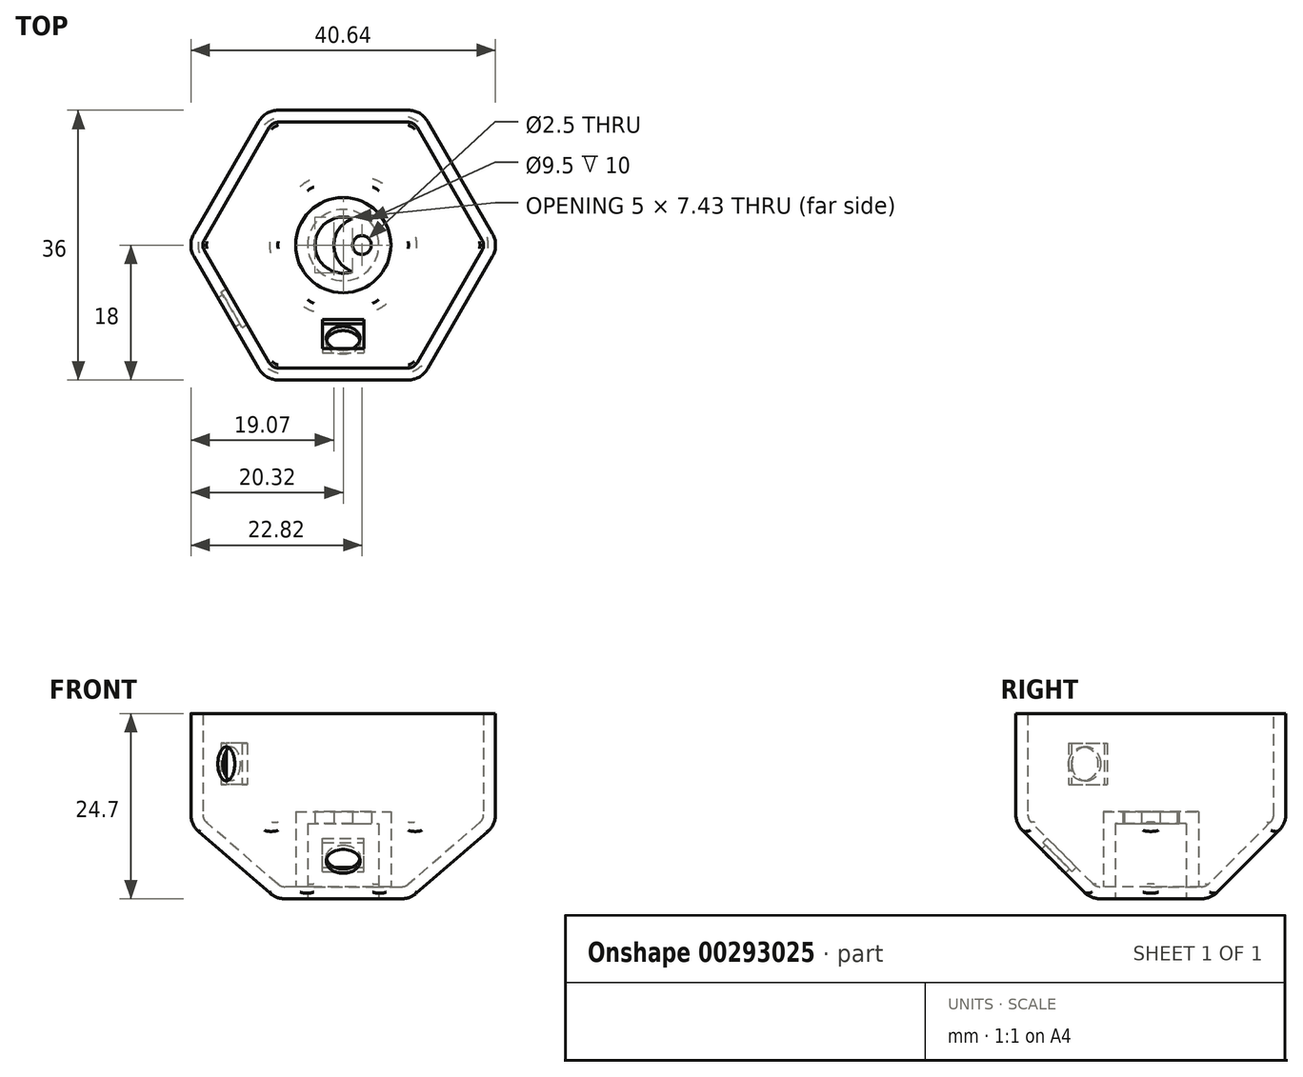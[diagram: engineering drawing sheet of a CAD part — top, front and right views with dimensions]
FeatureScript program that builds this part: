
annotation { "Feature Type Name" : "Feature", "Feature Type Description" : "" }
export const myFeature = defineFeature(function(context is Context, id is Id, definition is map)
    precondition{}
    {
        {
            var Q0;
            Q0=qCreatedBy(makeId("Top.planeOp"),FACE);
            var sketch = newSketch(context, id + "F0", { "sketchPlane" : qUnion([Q0])});
            skCircle(sketch, "E0.cCircle", {"center": v(0, 0) * mm, "radius": 18 * mm, "construction": true});
            skLineSegment(sketch, "E0.0", {"start": v(-10.4, 18) * mm, "end": v(10.4, 18) * mm});
            skLineSegment(sketch, "E0.1", {"start": v(10.4, 18) * mm, "end": v(20.78, 0) * mm});
            skLineSegment(sketch, "E0.2", {"start": v(20.78, 0) * mm, "end": v(10.4, -18) * mm});
            skLineSegment(sketch, "E0.3", {"start": v(10.4, -18) * mm, "end": v(-10.4, -18) * mm});
            skLineSegment(sketch, "E0.4", {"start": v(-10.4, -18) * mm, "end": v(-20.78, 0) * mm});
            skLineSegment(sketch, "E0.5", {"start": v(-20.78, 0) * mm, "end": v(-10.4, 18) * mm});
            skPoint(sketch, "E0.0.midPoint", {"position": v(0, 18) * mm});
            skSolve(sketch);
        }
        {
            var Q0;
            Q0 = qSketchRegion(id + "F0", true);
            extrude(context, id + "F1", {"entities" : qUnion([Q0]), "endBound" : BoundingType.SYMMETRIC, "depth" : 36 * mm});
        }
        {
            var Q0;
            Q0=makeQuery(id+"F1.opExtrude","CAP_FACE",FACE,{"disambiguationData":[OSD([sQuery(id+"F0.wireOp",EDGE,"E0.0"),sQuery(id+"F0.wireOp",EDGE,"E0.1"),sQuery(id+"F0.wireOp",EDGE,"E0.2"),sQuery(id+"F0.wireOp",EDGE,"E0.3"),sQuery(id+"F0.wireOp",EDGE,"E0.4"),sQuery(id+"F0.wireOp",EDGE,"E0.5")])],"isStart":false});
            var Q1;
            Q1=makeQuery(id+"F1.opExtrude","CAP_FACE",FACE,{"disambiguationData":[OSD([sQuery(id+"F0.wireOp",EDGE,"E0.0"),sQuery(id+"F0.wireOp",EDGE,"E0.1"),sQuery(id+"F0.wireOp",EDGE,"E0.2"),sQuery(id+"F0.wireOp",EDGE,"E0.3"),sQuery(id+"F0.wireOp",EDGE,"E0.4"),sQuery(id+"F0.wireOp",EDGE,"E0.5")])],"isStart":true});
            chamfer(context, id + "F2", {"entities" : qUnion([Q0, Q1]), "chamferType" : ChamferType.OFFSET_ANGLE, "width" : 10 * mm, "oppositeDirection" : false, "angle" : 45 * degree, "tangentPropagation" : true});
        }
        {
            var Q0;
            Q0=makeQuery(id+"F1.opExtrude","CAP_FACE",FACE,{"disambiguationData":[OSD([sQuery(id+"F0.wireOp",EDGE,"E0.0"),sQuery(id+"F0.wireOp",EDGE,"E0.1"),sQuery(id+"F0.wireOp",EDGE,"E0.2"),sQuery(id+"F0.wireOp",EDGE,"E0.3"),sQuery(id+"F0.wireOp",EDGE,"E0.4"),sQuery(id+"F0.wireOp",EDGE,"E0.5")])],"isStart":true});
            var sketch = newSketch(context, id + "F3", { "sketchPlane" : qUnion([Q0])});
            skCircle(sketch, "E1", {"center": v(0, 0) * mm, "radius": 4.75 * mm});
            skSolve(sketch);
        }
        {
            var Q0;
            Q0 = qSketchRegion(id + "F3", true);
            extrude(context, id + "F4", {"entities" : qUnion([Q0]), "operationType" : NewBodyOperationType.REMOVE, "oppositeDirection" : true, "depth" : 10 * mm});
        }
        {
            var Q0;
            Q0=makeQuery(id+"F4.boolean.opBoolean","COPY",FACE,{"derivedFrom":makeQuery(id+"F4.opExtrude","CAP_FACE",FACE,{"disambiguationData":[OSD([sQuery(id+"F3.wireOp",EDGE,"E1")])],"isStart":false})});
            var sketch = newSketch(context, id + "F5", { "sketchPlane" : qUnion([Q0])});
            skCircle(sketch, "E2", {"center": v(2.5, 0) * mm, "radius": 1.25 * mm});
            skSolve(sketch);
        }
        {
            var Q0;
            Q0 = qSketchRegion(id + "F5", true);
            extrude(context, id + "F6", {"entities" : qUnion([Q0]), "operationType" : NewBodyOperationType.REMOVE, "oppositeDirection" : true, "depth" : 60 * mm});
        }
        {
            var Q0;
            {var subQ0=sQuery(id+"F0.wireOp",EDGE,"E0.3");Q0=makeQuery(id+"F2.opChamfer","BLEND_FACE",FACE,{"disambiguationData":[OSD([subQ0]),TDD([makeQuery(id+"F1.opExtrude","CAP_EDGE",EDGE,{"disambiguationData":[OSD([subQ0])],"isStart":true})])]});}
            var sketch = newSketch(context, id + "F7", { "sketchPlane" : qUnion([Q0])});
            skCircle(sketch, "E3", {"center": v(0, 0) * mm, "radius": 2.25 * mm});
            skSolve(sketch);
        }
        {
            var Q0;
            Q0=makeQuery(id+"F1.opExtrude","SWEPT_FACE",FACE,{"disambiguationData":[OSD([sQuery(id+"F0.wireOp",EDGE,"E0.4")])]});
            var sketch = newSketch(context, id + "F8", { "sketchPlane" : qUnion([Q0])});
            skCircle(sketch, "E4", {"center": v(0, 0) * mm, "radius": 2.25 * mm});
            skSolve(sketch);
        }
        {
            var Q0;
            {var subQ0=sQuery(id+"F0.wireOp",EDGE,"E0.4");Q0=makeQuery(id+"F2.opChamfer","BLEND_EDGE",EDGE,{"blendedFrom":[makeQuery(id+"F1.opExtrude","CAP_EDGE",EDGE,{"disambiguationData":[OSD([subQ0])],"isStart":false}),makeQuery(id+"F1.opExtrude","SWEPT_FACE",FACE,{"disambiguationData":[OSD([subQ0])]})],"blendedInto":[makeQuery(id+"F1.opExtrude","SWEPT_FACE",FACE,{"disambiguationData":[OSD([subQ0])]})]});}
            var Q1;
            {var subQ0=sQuery(id+"F0.wireOp",EDGE,"E0.3");Q1=makeQuery(id+"F2.opChamfer","BLEND_EDGE",EDGE,{"blendedFrom":[makeQuery(id+"F1.opExtrude","CAP_EDGE",EDGE,{"disambiguationData":[OSD([subQ0])],"isStart":false}),makeQuery(id+"F1.opExtrude","SWEPT_FACE",FACE,{"disambiguationData":[OSD([subQ0])]})],"blendedInto":[makeQuery(id+"F1.opExtrude","SWEPT_FACE",FACE,{"disambiguationData":[OSD([subQ0])]})]});}
            var Q2;
            {var subQ0=sQuery(id+"F0.wireOp",EDGE,"E0.5");Q2=makeQuery(id+"F2.opChamfer","BLEND_EDGE",EDGE,{"blendedFrom":[makeQuery(id+"F1.opExtrude","CAP_EDGE",EDGE,{"disambiguationData":[OSD([subQ0])],"isStart":false}),makeQuery(id+"F1.opExtrude","SWEPT_FACE",FACE,{"disambiguationData":[OSD([subQ0])]})],"blendedInto":[makeQuery(id+"F1.opExtrude","SWEPT_FACE",FACE,{"disambiguationData":[OSD([subQ0])]})]});}
            var Q3;
            {var subQ0=sQuery(id+"F0.wireOp",EDGE,"E0.0");Q3=makeQuery(id+"F2.opChamfer","BLEND_EDGE",EDGE,{"blendedFrom":[makeQuery(id+"F1.opExtrude","CAP_EDGE",EDGE,{"disambiguationData":[OSD([subQ0])],"isStart":false}),makeQuery(id+"F1.opExtrude","SWEPT_FACE",FACE,{"disambiguationData":[OSD([subQ0])]})],"blendedInto":[makeQuery(id+"F1.opExtrude","SWEPT_FACE",FACE,{"disambiguationData":[OSD([subQ0])]})]});}
            var Q4;
            {var subQ0=sQuery(id+"F0.wireOp",EDGE,"E0.1");Q4=makeQuery(id+"F2.opChamfer","BLEND_EDGE",EDGE,{"blendedFrom":[makeQuery(id+"F1.opExtrude","CAP_EDGE",EDGE,{"disambiguationData":[OSD([subQ0])],"isStart":false}),makeQuery(id+"F1.opExtrude","SWEPT_FACE",FACE,{"disambiguationData":[OSD([subQ0])]})],"blendedInto":[makeQuery(id+"F1.opExtrude","SWEPT_FACE",FACE,{"disambiguationData":[OSD([subQ0])]})]});}
            var Q5;
            {var subQ0=sQuery(id+"F0.wireOp",EDGE,"E0.2");Q5=makeQuery(id+"F2.opChamfer","BLEND_EDGE",EDGE,{"blendedFrom":[makeQuery(id+"F1.opExtrude","CAP_EDGE",EDGE,{"disambiguationData":[OSD([subQ0])],"isStart":false}),makeQuery(id+"F1.opExtrude","SWEPT_FACE",FACE,{"disambiguationData":[OSD([subQ0])]})],"blendedInto":[makeQuery(id+"F1.opExtrude","SWEPT_FACE",FACE,{"disambiguationData":[OSD([subQ0])]})]});}
            var Q6;
            {var subQ0=sQuery(id+"F0.wireOp",EDGE,"E0.2");Q6=makeQuery(id+"F2.opChamfer","BLEND_EDGE",EDGE,{"blendedFrom":[makeQuery(id+"F1.opExtrude","CAP_EDGE",EDGE,{"disambiguationData":[OSD([subQ0])],"isStart":true}),makeQuery(id+"F1.opExtrude","SWEPT_FACE",FACE,{"disambiguationData":[OSD([subQ0])]})],"blendedInto":[makeQuery(id+"F1.opExtrude","SWEPT_FACE",FACE,{"disambiguationData":[OSD([subQ0])]})]});}
            var Q7;
            {var subQ0=sQuery(id+"F0.wireOp",EDGE,"E0.3");Q7=makeQuery(id+"F2.opChamfer","BLEND_EDGE",EDGE,{"blendedFrom":[makeQuery(id+"F1.opExtrude","CAP_EDGE",EDGE,{"disambiguationData":[OSD([subQ0])],"isStart":true}),makeQuery(id+"F1.opExtrude","SWEPT_FACE",FACE,{"disambiguationData":[OSD([subQ0])]})],"blendedInto":[makeQuery(id+"F1.opExtrude","SWEPT_FACE",FACE,{"disambiguationData":[OSD([subQ0])]})]});}
            var Q8;
            {var subQ0=sQuery(id+"F0.wireOp",EDGE,"E0.4");Q8=makeQuery(id+"F2.opChamfer","BLEND_EDGE",EDGE,{"blendedFrom":[makeQuery(id+"F1.opExtrude","CAP_EDGE",EDGE,{"disambiguationData":[OSD([subQ0])],"isStart":true}),makeQuery(id+"F1.opExtrude","SWEPT_FACE",FACE,{"disambiguationData":[OSD([subQ0])]})],"blendedInto":[makeQuery(id+"F1.opExtrude","SWEPT_FACE",FACE,{"disambiguationData":[OSD([subQ0])]})]});}
            var Q9;
            {var subQ0=sQuery(id+"F0.wireOp",EDGE,"E0.5");Q9=makeQuery(id+"F2.opChamfer","BLEND_EDGE",EDGE,{"blendedFrom":[makeQuery(id+"F1.opExtrude","CAP_EDGE",EDGE,{"disambiguationData":[OSD([subQ0])],"isStart":true}),makeQuery(id+"F1.opExtrude","SWEPT_FACE",FACE,{"disambiguationData":[OSD([subQ0])]})],"blendedInto":[makeQuery(id+"F1.opExtrude","SWEPT_FACE",FACE,{"disambiguationData":[OSD([subQ0])]})]});}
            var Q10;
            {var subQ0=sQuery(id+"F0.wireOp",EDGE,"E0.0");Q10=makeQuery(id+"F2.opChamfer","BLEND_EDGE",EDGE,{"blendedFrom":[makeQuery(id+"F1.opExtrude","CAP_EDGE",EDGE,{"disambiguationData":[OSD([subQ0])],"isStart":true}),makeQuery(id+"F1.opExtrude","SWEPT_FACE",FACE,{"disambiguationData":[OSD([subQ0])]})],"blendedInto":[makeQuery(id+"F1.opExtrude","SWEPT_FACE",FACE,{"disambiguationData":[OSD([subQ0])]})]});}
            var Q11;
            {var subQ0=sQuery(id+"F0.wireOp",EDGE,"E0.1");Q11=makeQuery(id+"F2.opChamfer","BLEND_EDGE",EDGE,{"blendedFrom":[makeQuery(id+"F1.opExtrude","CAP_EDGE",EDGE,{"disambiguationData":[OSD([subQ0])],"isStart":true}),makeQuery(id+"F1.opExtrude","SWEPT_FACE",FACE,{"disambiguationData":[OSD([subQ0])]})],"blendedInto":[makeQuery(id+"F1.opExtrude","SWEPT_FACE",FACE,{"disambiguationData":[OSD([subQ0])]})]});}
            fillet(context, id + "F9", {"entities" : qUnion([Q0, Q1, Q2, Q3, Q4, Q5, Q6, Q7, Q8, Q9, Q10, Q11]), "radius" : 3 * mm, "tangentPropagation" : true, "allowEdgeOverflow" : false});
        }
        {
            var Q0;
            Q0=makeQuery(id+"F2.opChamfer","BLEND_EDGE",EDGE,{"blendedFrom":[makeQuery(id+"F1.opExtrude","CAP_EDGE",EDGE,{"disambiguationData":[OSD([sQuery(id+"F0.wireOp",EDGE,"E0.4")])],"isStart":true}),makeQuery(id+"F1.opExtrude","CAP_EDGE",EDGE,{"disambiguationData":[OSD([sQuery(id+"F0.wireOp",EDGE,"E0.5")])],"isStart":true})],"blendedInto":[]});
            var Q1;
            Q1=makeQuery(id+"F2.opChamfer","BLEND_EDGE",EDGE,{"blendedFrom":[makeQuery(id+"F1.opExtrude","CAP_EDGE",EDGE,{"disambiguationData":[OSD([sQuery(id+"F0.wireOp",EDGE,"E0.0")])],"isStart":true}),makeQuery(id+"F1.opExtrude","CAP_EDGE",EDGE,{"disambiguationData":[OSD([sQuery(id+"F0.wireOp",EDGE,"E0.5")])],"isStart":true})],"blendedInto":[]});
            var Q2;
            {var subQ0=sQuery(id+"F0.wireOp",EDGE,"E0.5");Q2=makeQuery(id+"F2.opChamfer","BLEND_EDGE",EDGE,{"blendedFrom":[makeQuery(id+"F1.opExtrude","CAP_EDGE",EDGE,{"disambiguationData":[OSD([subQ0])],"isStart":true}),makeQuery(id+"F1.opExtrude","CAP_FACE",FACE,{"disambiguationData":[OSD([sQuery(id+"F0.wireOp",EDGE,"E0.0"),sQuery(id+"F0.wireOp",EDGE,"E0.1"),sQuery(id+"F0.wireOp",EDGE,"E0.2"),sQuery(id+"F0.wireOp",EDGE,"E0.3"),sQuery(id+"F0.wireOp",EDGE,"E0.4"),subQ0])],"isStart":true})],"blendedInto":[makeQuery(id+"F1.opExtrude","CAP_FACE",FACE,{"disambiguationData":[OSD([sQuery(id+"F0.wireOp",EDGE,"E0.0"),sQuery(id+"F0.wireOp",EDGE,"E0.1"),sQuery(id+"F0.wireOp",EDGE,"E0.2"),sQuery(id+"F0.wireOp",EDGE,"E0.3"),sQuery(id+"F0.wireOp",EDGE,"E0.4"),subQ0])],"isStart":true})]});}
            var Q3;
            {var subQ0=sQuery(id+"F0.wireOp",EDGE,"E0.4");Q3=makeQuery(id+"F2.opChamfer","BLEND_EDGE",EDGE,{"blendedFrom":[makeQuery(id+"F1.opExtrude","CAP_EDGE",EDGE,{"disambiguationData":[OSD([subQ0])],"isStart":true}),makeQuery(id+"F1.opExtrude","CAP_FACE",FACE,{"disambiguationData":[OSD([sQuery(id+"F0.wireOp",EDGE,"E0.0"),sQuery(id+"F0.wireOp",EDGE,"E0.1"),sQuery(id+"F0.wireOp",EDGE,"E0.2"),sQuery(id+"F0.wireOp",EDGE,"E0.3"),subQ0,sQuery(id+"F0.wireOp",EDGE,"E0.5")])],"isStart":true})],"blendedInto":[makeQuery(id+"F1.opExtrude","CAP_FACE",FACE,{"disambiguationData":[OSD([sQuery(id+"F0.wireOp",EDGE,"E0.0"),sQuery(id+"F0.wireOp",EDGE,"E0.1"),sQuery(id+"F0.wireOp",EDGE,"E0.2"),sQuery(id+"F0.wireOp",EDGE,"E0.3"),subQ0,sQuery(id+"F0.wireOp",EDGE,"E0.5")])],"isStart":true})]});}
            var Q4;
            Q4=makeQuery(id+"F2.opChamfer","BLEND_EDGE",EDGE,{"blendedFrom":[makeQuery(id+"F1.opExtrude","CAP_EDGE",EDGE,{"disambiguationData":[OSD([sQuery(id+"F0.wireOp",EDGE,"E0.3")])],"isStart":true}),makeQuery(id+"F1.opExtrude","CAP_EDGE",EDGE,{"disambiguationData":[OSD([sQuery(id+"F0.wireOp",EDGE,"E0.4")])],"isStart":true})],"blendedInto":[]});
            var Q5;
            {var subQ0=sQuery(id+"F0.wireOp",EDGE,"E0.3");Q5=makeQuery(id+"F2.opChamfer","BLEND_EDGE",EDGE,{"blendedFrom":[makeQuery(id+"F1.opExtrude","CAP_EDGE",EDGE,{"disambiguationData":[OSD([subQ0])],"isStart":true}),makeQuery(id+"F1.opExtrude","CAP_FACE",FACE,{"disambiguationData":[OSD([sQuery(id+"F0.wireOp",EDGE,"E0.0"),sQuery(id+"F0.wireOp",EDGE,"E0.1"),sQuery(id+"F0.wireOp",EDGE,"E0.2"),subQ0,sQuery(id+"F0.wireOp",EDGE,"E0.4"),sQuery(id+"F0.wireOp",EDGE,"E0.5")])],"isStart":true})],"blendedInto":[makeQuery(id+"F1.opExtrude","CAP_FACE",FACE,{"disambiguationData":[OSD([sQuery(id+"F0.wireOp",EDGE,"E0.0"),sQuery(id+"F0.wireOp",EDGE,"E0.1"),sQuery(id+"F0.wireOp",EDGE,"E0.2"),subQ0,sQuery(id+"F0.wireOp",EDGE,"E0.4"),sQuery(id+"F0.wireOp",EDGE,"E0.5")])],"isStart":true})]});}
            var Q6;
            {var subQ0=sQuery(id+"F0.wireOp",EDGE,"E0.0");Q6=makeQuery(id+"F2.opChamfer","BLEND_EDGE",EDGE,{"blendedFrom":[makeQuery(id+"F1.opExtrude","CAP_EDGE",EDGE,{"disambiguationData":[OSD([subQ0])],"isStart":true}),makeQuery(id+"F1.opExtrude","CAP_FACE",FACE,{"disambiguationData":[OSD([subQ0,sQuery(id+"F0.wireOp",EDGE,"E0.1"),sQuery(id+"F0.wireOp",EDGE,"E0.2"),sQuery(id+"F0.wireOp",EDGE,"E0.3"),sQuery(id+"F0.wireOp",EDGE,"E0.4"),sQuery(id+"F0.wireOp",EDGE,"E0.5")])],"isStart":true})],"blendedInto":[makeQuery(id+"F1.opExtrude","CAP_FACE",FACE,{"disambiguationData":[OSD([subQ0,sQuery(id+"F0.wireOp",EDGE,"E0.1"),sQuery(id+"F0.wireOp",EDGE,"E0.2"),sQuery(id+"F0.wireOp",EDGE,"E0.3"),sQuery(id+"F0.wireOp",EDGE,"E0.4"),sQuery(id+"F0.wireOp",EDGE,"E0.5")])],"isStart":true})]});}
            var Q7;
            Q7=makeQuery(id+"F2.opChamfer","BLEND_EDGE",EDGE,{"blendedFrom":[makeQuery(id+"F1.opExtrude","CAP_EDGE",EDGE,{"disambiguationData":[OSD([sQuery(id+"F0.wireOp",EDGE,"E0.0")])],"isStart":true}),makeQuery(id+"F1.opExtrude","CAP_EDGE",EDGE,{"disambiguationData":[OSD([sQuery(id+"F0.wireOp",EDGE,"E0.1")])],"isStart":true})],"blendedInto":[]});
            var Q8;
            Q8=makeQuery(id+"F2.opChamfer","BLEND_EDGE",EDGE,{"blendedFrom":[makeQuery(id+"F1.opExtrude","CAP_EDGE",EDGE,{"disambiguationData":[OSD([sQuery(id+"F0.wireOp",EDGE,"E0.2")])],"isStart":true}),makeQuery(id+"F1.opExtrude","CAP_EDGE",EDGE,{"disambiguationData":[OSD([sQuery(id+"F0.wireOp",EDGE,"E0.3")])],"isStart":true})],"blendedInto":[]});
            var Q9;
            {var subQ0=sQuery(id+"F0.wireOp",EDGE,"E0.2");Q9=makeQuery(id+"F2.opChamfer","BLEND_EDGE",EDGE,{"blendedFrom":[makeQuery(id+"F1.opExtrude","CAP_EDGE",EDGE,{"disambiguationData":[OSD([subQ0])],"isStart":true}),makeQuery(id+"F1.opExtrude","CAP_FACE",FACE,{"disambiguationData":[OSD([sQuery(id+"F0.wireOp",EDGE,"E0.0"),sQuery(id+"F0.wireOp",EDGE,"E0.1"),subQ0,sQuery(id+"F0.wireOp",EDGE,"E0.3"),sQuery(id+"F0.wireOp",EDGE,"E0.4"),sQuery(id+"F0.wireOp",EDGE,"E0.5")])],"isStart":true})],"blendedInto":[makeQuery(id+"F1.opExtrude","CAP_FACE",FACE,{"disambiguationData":[OSD([sQuery(id+"F0.wireOp",EDGE,"E0.0"),sQuery(id+"F0.wireOp",EDGE,"E0.1"),subQ0,sQuery(id+"F0.wireOp",EDGE,"E0.3"),sQuery(id+"F0.wireOp",EDGE,"E0.4"),sQuery(id+"F0.wireOp",EDGE,"E0.5")])],"isStart":true})]});}
            var Q10;
            Q10=makeQuery(id+"F2.opChamfer","BLEND_EDGE",EDGE,{"blendedFrom":[makeQuery(id+"F1.opExtrude","CAP_EDGE",EDGE,{"disambiguationData":[OSD([sQuery(id+"F0.wireOp",EDGE,"E0.1")])],"isStart":true}),makeQuery(id+"F1.opExtrude","CAP_EDGE",EDGE,{"disambiguationData":[OSD([sQuery(id+"F0.wireOp",EDGE,"E0.2")])],"isStart":true})],"blendedInto":[]});
            var Q11;
            {var subQ0=sQuery(id+"F0.wireOp",EDGE,"E0.1");Q11=makeQuery(id+"F2.opChamfer","BLEND_EDGE",EDGE,{"blendedFrom":[makeQuery(id+"F1.opExtrude","CAP_EDGE",EDGE,{"disambiguationData":[OSD([subQ0])],"isStart":true}),makeQuery(id+"F1.opExtrude","CAP_FACE",FACE,{"disambiguationData":[OSD([sQuery(id+"F0.wireOp",EDGE,"E0.0"),subQ0,sQuery(id+"F0.wireOp",EDGE,"E0.2"),sQuery(id+"F0.wireOp",EDGE,"E0.3"),sQuery(id+"F0.wireOp",EDGE,"E0.4"),sQuery(id+"F0.wireOp",EDGE,"E0.5")])],"isStart":true})],"blendedInto":[makeQuery(id+"F1.opExtrude","CAP_FACE",FACE,{"disambiguationData":[OSD([sQuery(id+"F0.wireOp",EDGE,"E0.0"),subQ0,sQuery(id+"F0.wireOp",EDGE,"E0.2"),sQuery(id+"F0.wireOp",EDGE,"E0.3"),sQuery(id+"F0.wireOp",EDGE,"E0.4"),sQuery(id+"F0.wireOp",EDGE,"E0.5")])],"isStart":true})]});}
            fillet(context, id + "F10", {"entities" : qUnion([Q0, Q1, Q2, Q3, Q4, Q5, Q6, Q7, Q8, Q9, Q10, Q11]), "radius" : 3 * mm, "tangentPropagation" : true, "allowEdgeOverflow" : false});
        }
        {
            var Q0;
            {var subQ0=sQuery(id+"F0.wireOp",EDGE,"E0.5");Q0=makeQuery(id+"F2.opChamfer","BLEND_EDGE",EDGE,{"blendedFrom":[makeQuery(id+"F1.opExtrude","CAP_EDGE",EDGE,{"disambiguationData":[OSD([subQ0])],"isStart":false}),makeQuery(id+"F1.opExtrude","CAP_FACE",FACE,{"disambiguationData":[OSD([sQuery(id+"F0.wireOp",EDGE,"E0.0"),sQuery(id+"F0.wireOp",EDGE,"E0.1"),sQuery(id+"F0.wireOp",EDGE,"E0.2"),sQuery(id+"F0.wireOp",EDGE,"E0.3"),sQuery(id+"F0.wireOp",EDGE,"E0.4"),subQ0])],"isStart":false})],"blendedInto":[makeQuery(id+"F1.opExtrude","CAP_FACE",FACE,{"disambiguationData":[OSD([sQuery(id+"F0.wireOp",EDGE,"E0.0"),sQuery(id+"F0.wireOp",EDGE,"E0.1"),sQuery(id+"F0.wireOp",EDGE,"E0.2"),sQuery(id+"F0.wireOp",EDGE,"E0.3"),sQuery(id+"F0.wireOp",EDGE,"E0.4"),subQ0])],"isStart":false})]});}
            var Q1;
            {var subQ0=sQuery(id+"F0.wireOp",EDGE,"E0.4");Q1=makeQuery(id+"F2.opChamfer","BLEND_EDGE",EDGE,{"blendedFrom":[makeQuery(id+"F1.opExtrude","CAP_EDGE",EDGE,{"disambiguationData":[OSD([subQ0])],"isStart":false}),makeQuery(id+"F1.opExtrude","CAP_FACE",FACE,{"disambiguationData":[OSD([sQuery(id+"F0.wireOp",EDGE,"E0.0"),sQuery(id+"F0.wireOp",EDGE,"E0.1"),sQuery(id+"F0.wireOp",EDGE,"E0.2"),sQuery(id+"F0.wireOp",EDGE,"E0.3"),subQ0,sQuery(id+"F0.wireOp",EDGE,"E0.5")])],"isStart":false})],"blendedInto":[makeQuery(id+"F1.opExtrude","CAP_FACE",FACE,{"disambiguationData":[OSD([sQuery(id+"F0.wireOp",EDGE,"E0.0"),sQuery(id+"F0.wireOp",EDGE,"E0.1"),sQuery(id+"F0.wireOp",EDGE,"E0.2"),sQuery(id+"F0.wireOp",EDGE,"E0.3"),subQ0,sQuery(id+"F0.wireOp",EDGE,"E0.5")])],"isStart":false})]});}
            fillet(context, id + "F11", {"entities" : qUnion([Q0, Q1]), "radius" : 3 * mm, "tangentPropagation" : true, "allowEdgeOverflow" : false});
        }
        {
            var Q0;
            Q0=makeQuery(id+"F1.opExtrude","CAP_FACE",FACE,{"disambiguationData":[OSD([sQuery(id+"F0.wireOp",EDGE,"E0.0"),sQuery(id+"F0.wireOp",EDGE,"E0.1"),sQuery(id+"F0.wireOp",EDGE,"E0.2"),sQuery(id+"F0.wireOp",EDGE,"E0.3"),sQuery(id+"F0.wireOp",EDGE,"E0.4"),sQuery(id+"F0.wireOp",EDGE,"E0.5")])],"isStart":false});
            var sketch = newSketch(context, id + "F12", { "sketchPlane" : qUnion([Q0])});
            skCircle(sketch, "E5", {"center": v(2.5, 0) * mm, "radius": 2.85 * mm});
            skSolve(sketch);
        }
        {
            var Q0;
            Q0 = qSketchRegion(id + "F12", true);
            extrude(context, id + "F13", {"entities" : qUnion([Q0]), "operationType" : NewBodyOperationType.REMOVE, "oppositeDirection" : true, "depth" : 3.5 * mm});
        }
        {
            var Q0;
            Q0=qCreatedBy(makeId("Top.planeOp"),FACE);
            cPlane(context, id + "F14", {"entities" : qUnion([Q0]), "cplaneType" : CPlaneType.OFFSET, "offset" : 6.7 * mm, "width" : 150 * mm, "height" : 150 * mm});
        }
        {
            var Q0;
            Q0=qCreatedBy(id+"F14.planeOp",FACE);
            var sketch = newSketch(context, id + "F15", { "sketchPlane" : qUnion([Q0])});
            skCircle(sketch, "E6", {"center": v(0, 0) * mm, "radius": 36.4 * mm});
            skSolve(sketch);
        }
        {
            var Q0;
            Q0 = qSketchRegion(id + "F15", true);
            extrude(context, id + "F16", {"entities" : qUnion([Q0]), "operationType" : NewBodyOperationType.REMOVE, "depth" : 25 * mm});
        }
        {
            var Q0;
            Q0=makeQuery(id+"F16.boolean.opBoolean","COPY",FACE,{"derivedFrom":makeQuery(id+"F16.opExtrude","CAP_FACE",FACE,{"disambiguationData":[OSD([sQuery(id+"F15.wireOp",EDGE,"E6")])],"isStart":true})});
            shell(context, id + "F17", {"entities" : qUnion([Q0]), "thickness" : 1.6 * mm});
        }
        {
            var Q0;
            {var subQ0=sQuery(id+"F3.wireOp",EDGE,"E1");Q0=makeQuery(id+"F17.opShell","OFFSET_FACE",FACE,{"disambiguationData":[OSD([subQ0]),TDD([makeQuery(id+"F4.boolean.opBoolean","COPY",FACE,{"derivedFrom":makeQuery(id+"F4.opExtrude","CAP_FACE",FACE,{"disambiguationData":[OSD([subQ0])],"isStart":false})})])]});}
            var sketch = newSketch(context, id + "F18", { "sketchPlane" : qUnion([Q0])});
            skCircle(sketch, "E7", {"center": v(0, 0) * mm, "radius": 6.64 * mm});
            skSolve(sketch);
        }
        {
            var Q0;
            Q0 = qSketchRegion(id + "F18", true);
            extrude(context, id + "F19", {"entities" : qUnion([Q0]), "operationType" : NewBodyOperationType.REMOVE, "depth" : 25 * mm});
        }
        {
            var Q0;
            Q0=makeQuery(id+"F4.boolean.opBoolean","COPY",FACE,{"derivedFrom":makeQuery(id+"F4.opExtrude","CAP_FACE",FACE,{"disambiguationData":[OSD([sQuery(id+"F3.wireOp",EDGE,"E1")])],"isStart":false})});
            var sketch = newSketch(context, id + "F20", { "sketchPlane" : qUnion([Q0])});
            skArc(sketch, "E8", {"start": v(1.25, 3.54) * mm, "mid": v(-1.25, 0) * mm, "end": v(1.25, -3.54) * mm});
            skArc(sketch, "E9", {"start": v(1.25, 3.54) * mm, "mid": v(-3.75, 0) * mm, "end": v(1.25, -3.54) * mm});
            skSolve(sketch);
        }
        {
            var Q0;
            Q0 = qSketchRegion(id + "F20", true);
            extrude(context, id + "F21", {"entities" : qUnion([Q0]), "operationType" : NewBodyOperationType.REMOVE, "oppositeDirection" : true, "depth" : 25 * mm});
        }
        {
            var Q0;
            Q0=makeQuery(id+"F7.imprint","IMPRINT",FACE,{"disambiguationData":[TD([[makeQuery(id+"F7.imprint","IMPRINT",EDGE,{"derivedFrom":sQuery(id+"F7.wireOp",EDGE,"E3")}),1.0]])]});
            var Q1;
            Q1=sQuery(id+"F7.wireOp",EDGE,"E3");
            extrude(context, id + "F22", {"entities" : qUnion([Q0]), "operationType" : NewBodyOperationType.REMOVE, "surfaceEntities" : qUnion([Q1]), "oppositeDirection" : true, "depth" : 5 * mm});
        }
        {
            var Q0;
            Q0=makeQuery(id+"F8.imprint","IMPRINT",FACE,{"disambiguationData":[TD([[makeQuery(id+"F8.imprint","IMPRINT",EDGE,{"derivedFrom":sQuery(id+"F8.wireOp",EDGE,"E4")}),1.0]])]});
            var Q1;
            Q1=sQuery(id+"F8.wireOp",EDGE,"E4");
            extrude(context, id + "F23", {"entities" : qUnion([Q0]), "operationType" : NewBodyOperationType.REMOVE, "surfaceEntities" : qUnion([Q1]), "oppositeDirection" : true, "depth" : 5 * mm});
        }
        {
            var Q0;
            {var subQ0=sQuery(id+"F0.wireOp",EDGE,"E0.3");Q0=makeQuery(id+"F17.opShell","OFFSET_FACE",FACE,{"disambiguationData":[OSD([subQ0]),TDD([makeQuery(id+"F2.opChamfer","BLEND_FACE",FACE,{"disambiguationData":[OSD([subQ0]),TDD([makeQuery(id+"F1.opExtrude","CAP_EDGE",EDGE,{"disambiguationData":[OSD([subQ0])],"isStart":true})])]})])]});}
            var sketch = newSketch(context, id + "F24", { "sketchPlane" : qUnion([Q0])});
            skLineSegment(sketch, "E10.bottom", {"start": v(2.75, -2.75) * mm, "end": v(-2.75, -2.75) * mm});
            skLineSegment(sketch, "E10.top", {"start": v(2.75, 2.75) * mm, "end": v(-2.75, 2.75) * mm});
            skLineSegment(sketch, "E10.left", {"start": v(2.75, -2.75) * mm, "end": v(2.75, 2.75) * mm});
            skLineSegment(sketch, "E10.right", {"start": v(-2.75, -2.75) * mm, "end": v(-2.75, 2.75) * mm});
            skSolve(sketch);
        }
        {
            var Q0;
            Q0 = qSketchRegion(id + "F24", true);
            extrude(context, id + "F25", {"entities" : qUnion([Q0]), "operationType" : NewBodyOperationType.REMOVE, "oppositeDirection" : true, "depth" : 0.8 * mm});
        }
        {
            var Q0;
            {var subQ0=sQuery(id+"F0.wireOp",EDGE,"E0.4");Q0=makeQuery(id+"F17.opShell","OFFSET_FACE",FACE,{"disambiguationData":[OSD([subQ0]),TDD([makeQuery(id+"F1.opExtrude","SWEPT_FACE",FACE,{"disambiguationData":[OSD([subQ0])]})])]});}
            var sketch = newSketch(context, id + "F26", { "sketchPlane" : qUnion([Q0])});
            skLineSegment(sketch, "E11.bottom", {"start": v(-2.75, 2.75) * mm, "end": v(2.75, 2.75) * mm});
            skLineSegment(sketch, "E11.top", {"start": v(-2.75, -2.75) * mm, "end": v(2.75, -2.75) * mm});
            skLineSegment(sketch, "E11.left", {"start": v(-2.75, 2.75) * mm, "end": v(-2.75, -2.75) * mm});
            skLineSegment(sketch, "E11.right", {"start": v(2.75, 2.75) * mm, "end": v(2.75, -2.75) * mm});
            skSolve(sketch);
        }
        {
            var Q0;
            Q0 = qSketchRegion(id + "F26", true);
            extrude(context, id + "F27", {"entities" : qUnion([Q0]), "operationType" : NewBodyOperationType.REMOVE, "oppositeDirection" : true, "depth" : 0.8 * mm});
        }
        {
            var Q0;
            Q0=qCreatedBy(makeId("Front.planeOp"),FACE);
            var sketch = newSketch(context, id + "F28", { "sketchPlane" : qUnion([Q0])});
            skLineSegment(sketch, "E12", {"start": v(0, 31.87) * mm, "end": v(0, -36.19) * mm, "construction": true});
            skSolve(sketch);
        }
    });
